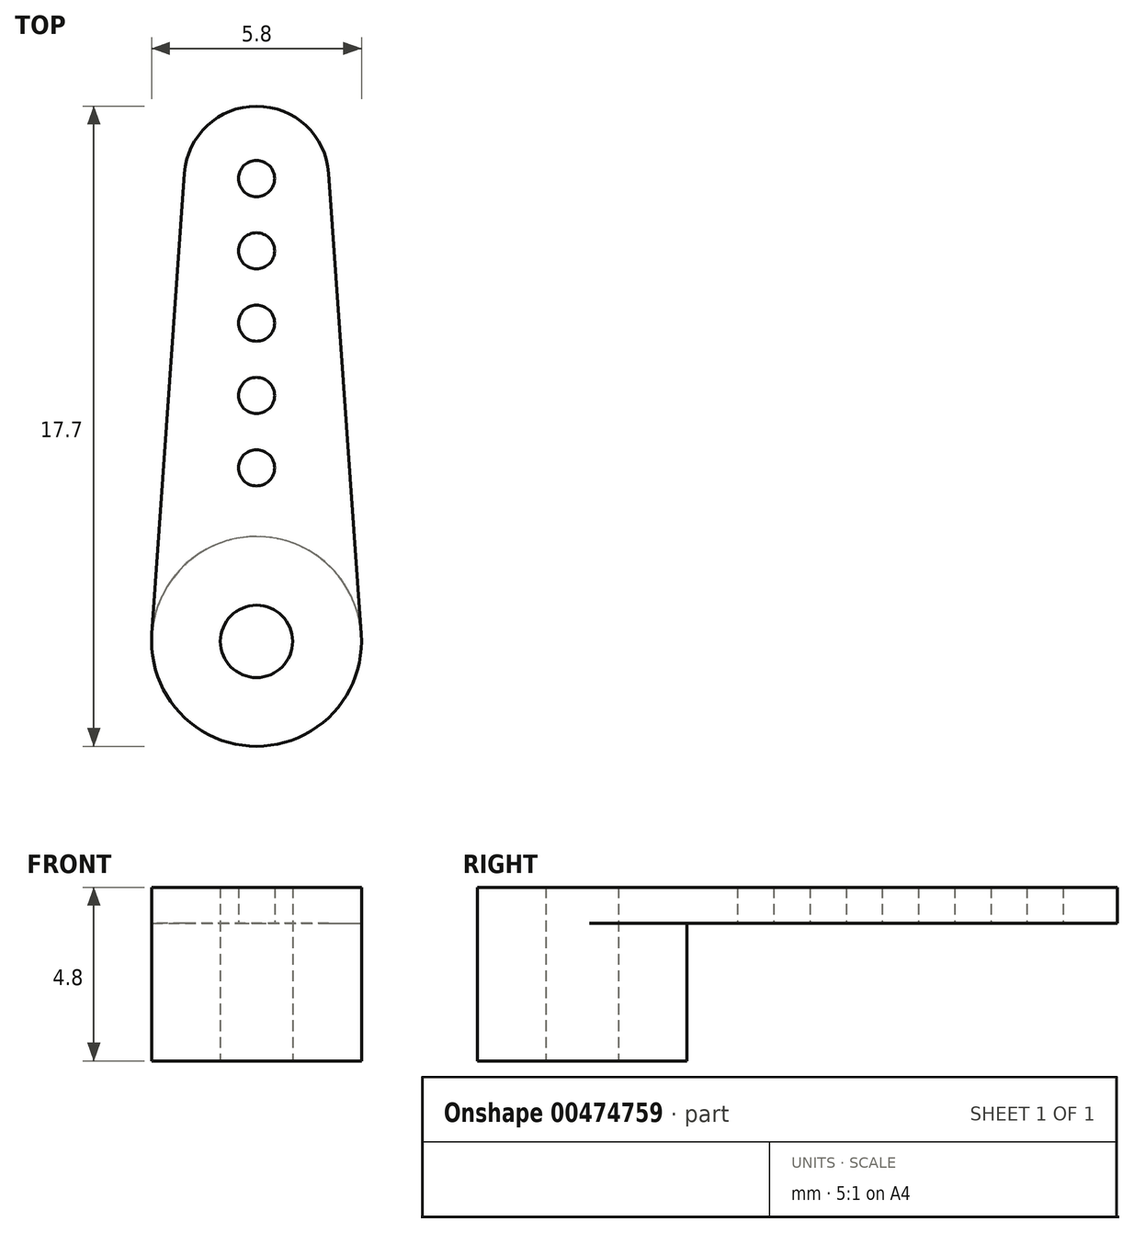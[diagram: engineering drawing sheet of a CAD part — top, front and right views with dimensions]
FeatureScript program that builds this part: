
annotation { "Feature Type Name" : "Feature", "Feature Type Description" : "" }
export const myFeature = defineFeature(function(context is Context, id is Id, definition is map)
    precondition{}
    {
        {
            var Q0;
            Q0=qCreatedBy(makeId("Top.planeOp"),FACE);
            var sketch = newSketch(context, id + "F0", { "sketchPlane" : qUnion([Q0])});
            skCircle(sketch, "E0", {"center": v(0, 0) * mm, "radius": 1 * mm});
            skArc(sketch, "E1", {"start": v(-2.9, 0.2) * mm, "mid": v(0, -2.9) * mm, "end": v(2.9, 0.2) * mm});
            skArc(sketch, "E2", {"start": v(2, 12.94) * mm, "mid": v(0, 14.8) * mm, "end": v(-2, 12.94) * mm});
            skLineSegment(sketch, "E3", {"start": v(-2, 12.94) * mm, "end": v(-2.9, 0.2) * mm});
            skLineSegment(sketch, "E4", {"start": v(2, 12.94) * mm, "end": v(2.9, 0.2) * mm});
            skCircle(sketch, "E5", {"center": v(0, 12.8) * mm, "radius": 0.5 * mm});
            skCircle(sketch, "E6", {"center": v(0, 10.8) * mm, "radius": 0.5 * mm});
            skCircle(sketch, "E7", {"center": v(0, 8.8) * mm, "radius": 0.5 * mm});
            skCircle(sketch, "E8", {"center": v(0, 6.8) * mm, "radius": 0.5 * mm});
            skCircle(sketch, "E9", {"center": v(0, 4.8) * mm, "radius": 0.5 * mm});
            skSolve(sketch);
        }
        {
            var Q0;
            Q0 = qSketchRegion(id + "F0", true);
            extrude(context, id + "F1", {"entities" : qUnion([Q0]), "depth" : 4.8 * mm, "offsetDistance" : 25 * mm});
        }
        {
            var Q0;
            Q0=makeQuery(id+"F1.opExtrude","CAP_FACE",FACE,{"disambiguationData":[OSD([sQuery(id+"F0.wireOp",EDGE,"E0"),sQuery(id+"F0.wireOp",EDGE,"E1"),sQuery(id+"F0.wireOp",EDGE,"E2"),sQuery(id+"F0.wireOp",EDGE,"E3"),sQuery(id+"F0.wireOp",EDGE,"E4"),sQuery(id+"F0.wireOp",EDGE,"E5"),sQuery(id+"F0.wireOp",EDGE,"E6"),sQuery(id+"F0.wireOp",EDGE,"E7"),sQuery(id+"F0.wireOp",EDGE,"E8"),sQuery(id+"F0.wireOp",EDGE,"E9")])],"isStart":true});
            var sketch = newSketch(context, id + "F2", { "sketchPlane" : qUnion([Q0])});
            skArc(sketch, "E10", {"start": v(-2.9, -0.2) * mm, "mid": v(0, -2.9) * mm, "end": v(2.9, -0.2) * mm});
            skLineSegment(sketch, "E11", {"start": v(-2.9, -0.2) * mm, "end": v(-2, -12.94) * mm});
            skLineSegment(sketch, "E12", {"start": v(2.9, -0.2) * mm, "end": v(2, -12.94) * mm});
            skArc(sketch, "E13", {"start": v(-2, -12.94) * mm, "mid": v(0, -14.8) * mm, "end": v(2, -12.94) * mm});
            skSolve(sketch);
        }
        {
            var Q0;
            Q0 = qSketchRegion(id + "F2", true);
            extrude(context, id + "F3", {"entities" : qUnion([Q0]), "operationType" : NewBodyOperationType.REMOVE, "oppositeDirection" : true, "depth" : 3.8 * mm, "offsetDistance" : 25 * mm});
        }
    });
